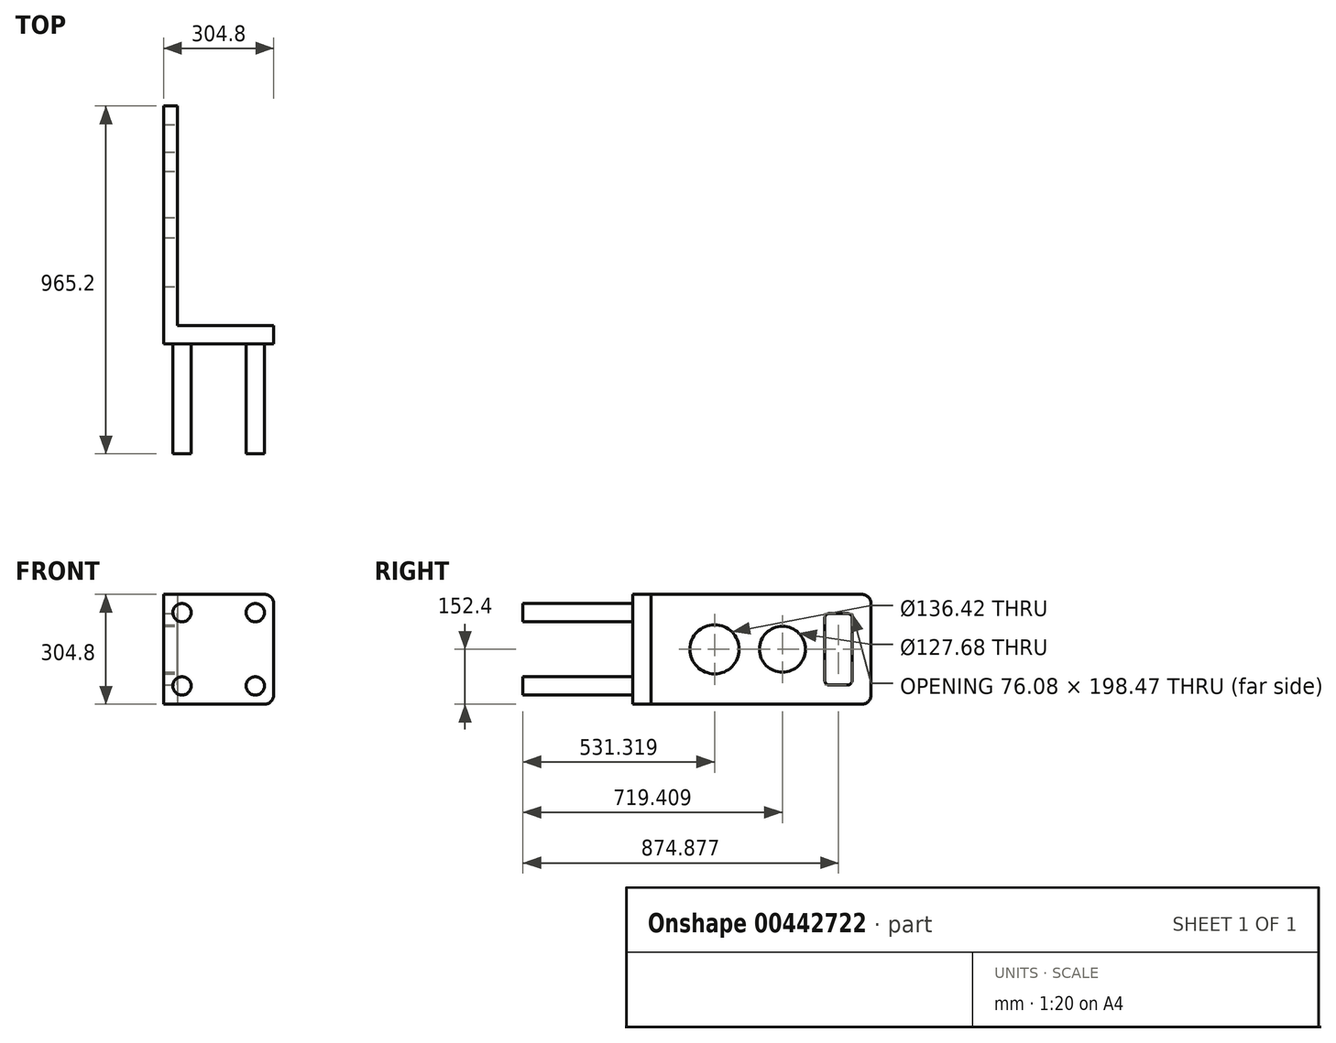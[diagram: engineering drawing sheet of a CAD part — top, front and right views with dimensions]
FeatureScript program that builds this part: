
annotation { "Feature Type Name" : "Feature", "Feature Type Description" : "" }
export const myFeature = defineFeature(function(context is Context, id is Id, definition is map)
    precondition{}
    {
        {
            var Q0;
            Q0=qCreatedBy(makeId("Front.planeOp"),FACE);
            var sketch = newSketch(context, id + "F0", { "sketchPlane" : qUnion([Q0])});
            skLineSegment(sketch, "E0.bottom", {"start": v(152.4, -152.4) * mm, "end": v(-152.4, -152.4) * mm});
            skLineSegment(sketch, "E0.top", {"start": v(152.4, 152.4) * mm, "end": v(-152.4, 152.4) * mm});
            skLineSegment(sketch, "E0.left", {"start": v(152.4, -152.4) * mm, "end": v(152.4, 152.4) * mm});
            skLineSegment(sketch, "E0.right", {"start": v(-152.4, -152.4) * mm, "end": v(-152.4, 152.4) * mm});
            skPoint(sketch, "E0.middle", {"position": v(0, 0) * mm});
            skSolve(sketch);
        }
        {
            var Q0;
            Q0=makeQuery(id+"F0.imprint","IMPRINT",FACE,{"disambiguationData":[TD([[makeQuery(id+"F0.imprint","IMPRINT",EDGE,{"derivedFrom":sQuery(id+"F0.wireOp",EDGE,"E0.bottom")}),-1.0]])]});
            extrude(context, id + "F1", {"entities" : qUnion([Q0]), "depth" : 50.8 * mm});
        }
        {
            var Q0;
            Q0=makeQuery(id+"F1.opExtrude","CAP_FACE",FACE,{"disambiguationData":[OSD([sQuery(id+"F0.wireOp",EDGE,"E0.bottom"),sQuery(id+"F0.wireOp",EDGE,"E0.top"),sQuery(id+"F0.wireOp",EDGE,"E0.left"),sQuery(id+"F0.wireOp",EDGE,"E0.right")])],"isStart":false});
            var sketch = newSketch(context, id + "F2", { "sketchPlane" : qUnion([Q0])});
            skCircle(sketch, "E1", {"center": v(-101.6, 101.6) * mm, "radius": 25.4 * mm});
            skSolve(sketch);
        }
        {
            var Q0;
            Q0=makeQuery(id+"F2.imprint","IMPRINT",FACE,{"disambiguationData":[TD([[makeQuery(id+"F2.imprint","IMPRINT",EDGE,{"derivedFrom":sQuery(id+"F2.wireOp",EDGE,"E1")}),1.0]])]});
            extrude(context, id + "F3", {"entities" : qUnion([Q0]), "depth" : 304.8 * mm});
        }
        {
            var Q0;
            Q0=makeQuery(id+"F3.opExtrude","SWEPT_BODY",BODY,{"disambiguationData":[OSD([sQuery(id+"F2.wireOp",EDGE,"E1")])]});
            var Q1;
            Q1=qCreatedBy(makeId("Top.planeOp"),FACE);
            mirror(context, id + "F4", {"entities" : qUnion([Q0]), "mirrorPlane" : qUnion([Q1])});
        }
        {
            var Q0;
            Q0=makeQuery(id+"F3.opExtrude","SWEPT_BODY",BODY,{"disambiguationData":[OSD([sQuery(id+"F2.wireOp",EDGE,"E1")])]});
            var Q1;
            Q1=makeQuery(id+"F4.opPattern","COPY",BODY,{"derivedFrom":makeQuery(id+"F3.opExtrude","SWEPT_BODY",BODY,{"disambiguationData":[OSD([sQuery(id+"F2.wireOp",EDGE,"E1")])]}),"instanceName":"1"});
            var Q2;
            Q2=qCreatedBy(makeId("Right.planeOp"),FACE);
            mirror(context, id + "F5", {"operationType" : NewBodyOperationType.ADD, "entities" : qUnion([Q0, Q1]), "mirrorPlane" : qUnion([Q2])});
        }
        {
            var Q0;
            Q0=makeQuery(id+"F1.opExtrude","CAP_FACE",FACE,{"disambiguationData":[OSD([sQuery(id+"F0.wireOp",EDGE,"E0.bottom"),sQuery(id+"F0.wireOp",EDGE,"E0.top"),sQuery(id+"F0.wireOp",EDGE,"E0.left"),sQuery(id+"F0.wireOp",EDGE,"E0.right")])],"isStart":true});
            var sketch = newSketch(context, id + "F6", { "sketchPlane" : qUnion([Q0])});
            skLineSegment(sketch, "E2.bottom", {"start": v(152.4, 152.4) * mm, "end": v(114.3, 152.4) * mm});
            skLineSegment(sketch, "E2.top", {"start": v(152.4, -152.4) * mm, "end": v(114.3, -152.4) * mm});
            skLineSegment(sketch, "E2.left", {"start": v(152.4, 152.4) * mm, "end": v(152.4, -152.4) * mm});
            skLineSegment(sketch, "E2.right", {"start": v(114.3, 152.4) * mm, "end": v(114.3, -152.4) * mm});
            skSolve(sketch);
        }
        {
            var Q0;
            Q0=makeQuery(id+"F6.imprint","IMPRINT",FACE,{"disambiguationData":[TD([[makeQuery(id+"F6.imprint","IMPRINT",EDGE,{"derivedFrom":sQuery(id+"F6.wireOp",EDGE,"E2.bottom")}),-1.0]])]});
            extrude(context, id + "F7", {"entities" : qUnion([Q0]), "operationType" : NewBodyOperationType.ADD, "depth" : 609.6 * mm});
        }
        {
            var Q0;
            Q0=makeQuery(id+"F7.opExtrude","CAP_EDGE",EDGE,{"disambiguationData":[OSD([sQuery(id+"F6.wireOp",EDGE,"E2.bottom")])],"isStart":false});
            var Q1;
            Q1=makeQuery(id+"F7.opExtrude","CAP_EDGE",EDGE,{"disambiguationData":[OSD([sQuery(id+"F6.wireOp",EDGE,"E2.top")])],"isStart":false});
            fillet(context, id + "F8", {"entities" : qUnion([Q0, Q1]), "radius" : 25.4 * mm, "tangentPropagation" : true, "allowEdgeOverflow" : false});
        }
        {
            var Q0;
            Q0=makeQuery(id+"F7.opExtrude","CAP_EDGE",EDGE,{"disambiguationData":[OSD([sQuery(id+"F6.wireOp",EDGE,"E2.right")])],"isStart":true});
            var Q1;
            Q1=makeQuery(id+"F1.opExtrude","SWEPT_EDGE",EDGE,{"disambiguationData":[OSD([sQuery(id+"F0.wireOp",EDGE,"E0.top"),sQuery(id+"F0.wireOp",EDGE,"E0.left")])]});
            fillet(context, id + "F9", {"entities" : qUnion([Q0, Q1]), "radius" : 25.4 * mm, "tangentPropagation" : true, "allowEdgeOverflow" : false});
        }
        {
            var Q0;
            Q0=makeQuery(id+"F1.opExtrude","SWEPT_EDGE",EDGE,{"disambiguationData":[OSD([sQuery(id+"F0.wireOp",EDGE,"E0.top"),sQuery(id+"F0.wireOp",EDGE,"E0.left")])]});
            var Q1;
            Q1=makeQuery(id+"F1.opExtrude","SWEPT_EDGE",EDGE,{"disambiguationData":[OSD([sQuery(id+"F0.wireOp",EDGE,"E0.bottom"),sQuery(id+"F0.wireOp",EDGE,"E0.left")])]});
            fillet(context, id + "F10", {"entities" : qUnion([Q0, Q1]), "radius" : 25.4 * mm, "tangentPropagation" : true, "allowEdgeOverflow" : false});
        }
        {
            var Q0;
            Q0=makeQuery(id+"F7.opExtrude","SWEPT_FACE",FACE,{"disambiguationData":[OSD([sQuery(id+"F6.wireOp",EDGE,"E2.right")])]});
            var sketch = newSketch(context, id + "F11", { "sketchPlane" : qUnion([Q0])});
            skCircle(sketch, "E3", {"center": v(175.72, 0) * mm, "radius": 68.21 * mm});
            skSolve(sketch);
        }
        {
            var Q0;
            Q0=makeQuery(id+"F11.imprint","IMPRINT",FACE,{"disambiguationData":[TD([[makeQuery(id+"F11.imprint","IMPRINT",EDGE,{"derivedFrom":sQuery(id+"F11.wireOp",EDGE,"E3")}),1.0]])]});
            extrude(context, id + "F12", {"entities" : qUnion([Q0]), "operationType" : NewBodyOperationType.REMOVE, "endBound" : BoundingType.UP_TO_NEXT, "oppositeDirection" : true, "depth" : 25.4 * mm});
        }
        {
            var Q0;
            Q0=makeQuery(id+"F7.opExtrude","SWEPT_FACE",FACE,{"disambiguationData":[OSD([sQuery(id+"F6.wireOp",EDGE,"E2.right")])]});
            var sketch = newSketch(context, id + "F13", { "sketchPlane" : qUnion([Q0])});
            skCircle(sketch, "E4", {"center": v(363.8, 0) * mm, "radius": 63.84 * mm});
            skSolve(sketch);
        }
        {
            var Q0;
            Q0=makeQuery(id+"F13.imprint","IMPRINT",FACE,{"disambiguationData":[TD([[makeQuery(id+"F13.imprint","IMPRINT",EDGE,{"derivedFrom":sQuery(id+"F13.wireOp",EDGE,"E4")}),1.0]])]});
            extrude(context, id + "F14", {"entities" : qUnion([Q0]), "operationType" : NewBodyOperationType.REMOVE, "endBound" : BoundingType.UP_TO_NEXT, "oppositeDirection" : true, "depth" : 25.4 * mm});
        }
        {
            var Q0;
            Q0=makeQuery(id+"F7.opExtrude","SWEPT_FACE",FACE,{"disambiguationData":[OSD([sQuery(id+"F6.wireOp",EDGE,"E2.right")])]});
            var sketch = newSketch(context, id + "F15", { "sketchPlane" : qUnion([Q0])});
            skLineSegment(sketch, "E5.bottom", {"start": v(481.24, -99.23) * mm, "end": v(557.32, -99.23) * mm});
            skLineSegment(sketch, "E5.top", {"start": v(481.24, 99.23) * mm, "end": v(557.32, 99.23) * mm});
            skLineSegment(sketch, "E5.left", {"start": v(481.24, -99.23) * mm, "end": v(481.24, 99.23) * mm});
            skLineSegment(sketch, "E5.right", {"start": v(557.32, -99.23) * mm, "end": v(557.32, 99.23) * mm});
            skPoint(sketch, "E5.middle", {"position": v(519.28, 0) * mm});
            skSolve(sketch);
        }
        {
            var Q0;
            Q0=makeQuery(id+"F15.imprint","IMPRINT",FACE,{"disambiguationData":[TD([[makeQuery(id+"F15.imprint","IMPRINT",EDGE,{"derivedFrom":sQuery(id+"F15.wireOp",EDGE,"E5.bottom")}),1.0]])]});
            extrude(context, id + "F16", {"entities" : qUnion([Q0]), "operationType" : NewBodyOperationType.REMOVE, "endBound" : BoundingType.UP_TO_NEXT, "oppositeDirection" : true, "depth" : 25.4 * mm});
        }
        {
            var Q0;
            Q0=makeQuery(id+"F16.boolean.opBoolean","COPY",EDGE,{"derivedFrom":makeQuery(id+"F16.opExtrude","SWEPT_EDGE",EDGE,{"disambiguationData":[OSD([sQuery(id+"F15.wireOp",EDGE,"E5.bottom"),sQuery(id+"F15.wireOp",EDGE,"E5.right")])]})});
            var Q1;
            Q1=makeQuery(id+"F16.boolean.opBoolean","COPY",EDGE,{"derivedFrom":makeQuery(id+"F16.opExtrude","SWEPT_EDGE",EDGE,{"disambiguationData":[OSD([sQuery(id+"F15.wireOp",EDGE,"E5.top"),sQuery(id+"F15.wireOp",EDGE,"E5.right")])]})});
            var Q2;
            Q2=makeQuery(id+"F16.boolean.opBoolean","COPY",EDGE,{"derivedFrom":makeQuery(id+"F16.opExtrude","SWEPT_EDGE",EDGE,{"disambiguationData":[OSD([sQuery(id+"F15.wireOp",EDGE,"E5.top"),sQuery(id+"F15.wireOp",EDGE,"E5.left")])]})});
            var Q3;
            Q3=makeQuery(id+"F16.boolean.opBoolean","COPY",EDGE,{"derivedFrom":makeQuery(id+"F16.opExtrude","SWEPT_EDGE",EDGE,{"disambiguationData":[OSD([sQuery(id+"F15.wireOp",EDGE,"E5.bottom"),sQuery(id+"F15.wireOp",EDGE,"E5.left")])]})});
            fillet(context, id + "F17", {"entities" : qUnion([Q0, Q1, Q2, Q3]), "radius" : 12.7 * mm, "tangentPropagation" : true, "allowEdgeOverflow" : false});
        }
    });
